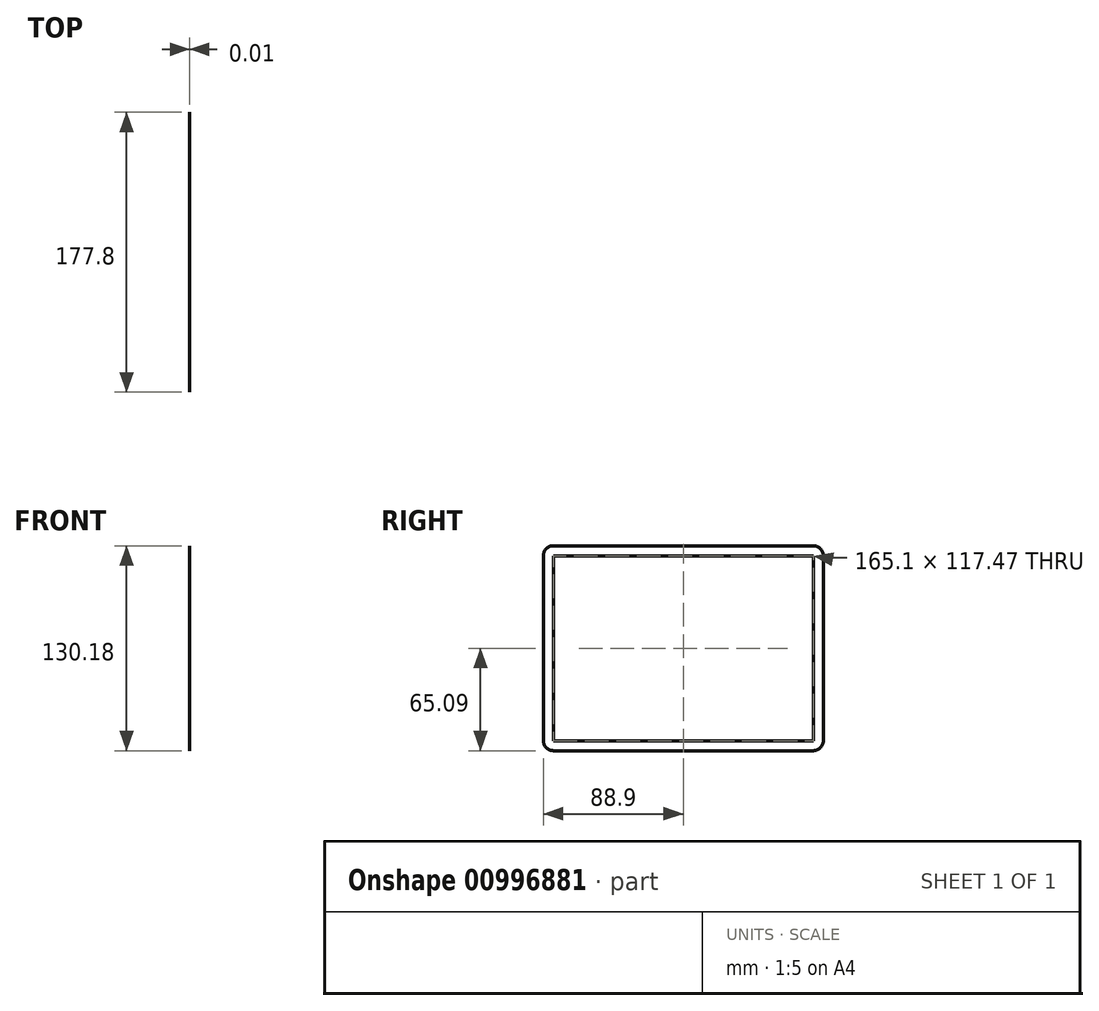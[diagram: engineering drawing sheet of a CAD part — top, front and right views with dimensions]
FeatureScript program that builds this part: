
annotation { "Feature Type Name" : "Feature", "Feature Type Description" : "" }
export const myFeature = defineFeature(function(context is Context, id is Id, definition is map)
    precondition{}
    {
        {
            var Q0;
            Q0=qCreatedBy(makeId("Right.planeOp"),FACE);
            var sketch = newSketch(context, id + "F0", { "sketchPlane" : qUnion([Q0])});
            skLineSegment(sketch, "E0.bottom", {"start": v(82.55, 53.98) * mm, "end": v(-82.55, 53.98) * mm});
            skLineSegment(sketch, "E0.top", {"start": v(82.55, -53.97) * mm, "end": v(-82.55, -53.97) * mm});
            skLineSegment(sketch, "E0.left", {"start": v(82.55, 53.98) * mm, "end": v(82.55, -53.97) * mm});
            skLineSegment(sketch, "E0.right", {"start": v(-82.55, 53.98) * mm, "end": v(-82.55, -53.97) * mm});
            skPoint(sketch, "E0.middle", {"position": v(0, 0) * mm});
            skLineSegment(sketch, "E1.bottom", {"start": v(82.55, 58.74) * mm, "end": v(-82.55, 58.74) * mm});
            skLineSegment(sketch, "E1.top", {"start": v(82.55, -58.74) * mm, "end": v(-82.55, -58.74) * mm});
            skLineSegment(sketch, "E1.left", {"start": v(82.55, 58.74) * mm, "end": v(82.55, -58.74) * mm});
            skLineSegment(sketch, "E1.right", {"start": v(-82.55, 58.74) * mm, "end": v(-82.55, -58.74) * mm});
            skLineSegment(sketch, "E2.bottom", {"start": v(82.55, 65.09) * mm, "end": v(-82.55, 65.09) * mm});
            skLineSegment(sketch, "E2.top", {"start": v(82.55, -65.09) * mm, "end": v(-82.55, -65.09) * mm});
            skLineSegment(sketch, "E2.left", {"start": v(88.9, 58.74) * mm, "end": v(88.9, -58.74) * mm});
            skLineSegment(sketch, "E2.right", {"start": v(-88.9, 58.74) * mm, "end": v(-88.9, -58.74) * mm});
            skPoint(sketch, "E3.visualSharp", {"position": v(-88.9, 65.09) * mm});
            skArc(sketch, "E3.filletArc", {"start": v(-82.55, 65.09) * mm, "mid": v(-87.04, 63.23) * mm, "end": v(-88.9, 58.74) * mm});
            skPoint(sketch, "E4.visualSharp", {"position": v(88.9, 65.09) * mm});
            skArc(sketch, "E4.filletArc", {"start": v(88.9, 58.74) * mm, "mid": v(87.04, 63.23) * mm, "end": v(82.55, 65.09) * mm});
            skPoint(sketch, "E5.visualSharp", {"position": v(88.9, -65.09) * mm});
            skArc(sketch, "E5.filletArc", {"start": v(82.55, -65.09) * mm, "mid": v(87.04, -63.23) * mm, "end": v(88.9, -58.74) * mm});
            skPoint(sketch, "E6.visualSharp", {"position": v(-88.9, -65.09) * mm});
            skArc(sketch, "E6.filletArc", {"start": v(-88.9, -58.74) * mm, "mid": v(-87.04, -63.23) * mm, "end": v(-82.55, -65.09) * mm});
            skLineSegment(sketch, "E7", {"start": v(0, 65.09) * mm, "end": v(0, -65.09) * mm, "construction": true});
            skPoint(sketch, "E8", {"position": v(0, 65.09) * mm});
            skPoint(sketch, "E9", {"position": v(0, 58.74) * mm});
            skPoint(sketch, "E10", {"position": v(0, 53.98) * mm});
            skPoint(sketch, "E11", {"position": v(0, -53.97) * mm});
            skPoint(sketch, "E12", {"position": v(0, -58.74) * mm});
            skPoint(sketch, "E13", {"position": v(0, -65.09) * mm});
            skLineSegment(sketch, "E14.bottom", {"start": v(-82.55, 58.74) * mm, "end": v(-74.61, 58.74) * mm});
            skLineSegment(sketch, "E14.top", {"start": v(-82.55, 53.98) * mm, "end": v(-74.61, 53.98) * mm});
            skLineSegment(sketch, "E14.left", {"start": v(-82.55, 58.74) * mm, "end": v(-82.55, 53.98) * mm});
            skLineSegment(sketch, "E14.right", {"start": v(-74.61, 58.74) * mm, "end": v(-74.61, 53.98) * mm});
            skLineSegment(sketch, "E15.bottom", {"start": v(82.55, 58.74) * mm, "end": v(74.61, 58.74) * mm});
            skLineSegment(sketch, "E15.top", {"start": v(82.55, 53.98) * mm, "end": v(74.61, 53.98) * mm});
            skLineSegment(sketch, "E15.left", {"start": v(82.55, 58.74) * mm, "end": v(82.55, 53.98) * mm});
            skLineSegment(sketch, "E15.right", {"start": v(74.61, 58.74) * mm, "end": v(74.61, 53.98) * mm});
            skLineSegment(sketch, "E16.bottom", {"start": v(82.55, -58.74) * mm, "end": v(74.61, -58.74) * mm});
            skLineSegment(sketch, "E16.top", {"start": v(82.55, -53.97) * mm, "end": v(74.61, -53.97) * mm});
            skLineSegment(sketch, "E16.left", {"start": v(82.55, -58.74) * mm, "end": v(82.55, -53.97) * mm});
            skLineSegment(sketch, "E16.right", {"start": v(74.61, -58.74) * mm, "end": v(74.61, -53.97) * mm});
            skLineSegment(sketch, "E17.bottom", {"start": v(-82.55, -58.74) * mm, "end": v(-74.61, -58.74) * mm});
            skLineSegment(sketch, "E17.top", {"start": v(-82.55, -53.97) * mm, "end": v(-74.61, -53.97) * mm});
            skLineSegment(sketch, "E17.left", {"start": v(-82.55, -58.74) * mm, "end": v(-82.55, -53.97) * mm});
            skLineSegment(sketch, "E17.right", {"start": v(-74.61, -58.74) * mm, "end": v(-74.61, -53.97) * mm});
            skSolve(sketch);
        }
        {
            var Q0;
            {var subQ6=sQuery(id+"F0.wireOp",EDGE,"E1.bottom");Q0=makeQuery(id+"F0.imprint","IMPRINT",FACE,{"disambiguationData":[TD([[makeQuery(id+"F0.imprint","IMPRINT",EDGE,{"derivedFrom":subQ6}),-1.0]])]});}
            extrude(context, id + "F1", {"entities" : qUnion([Q0]), "depth" : 3 / 203.2 * mm, "offsetDistance" : 25.4 * mm});
        }
    });
